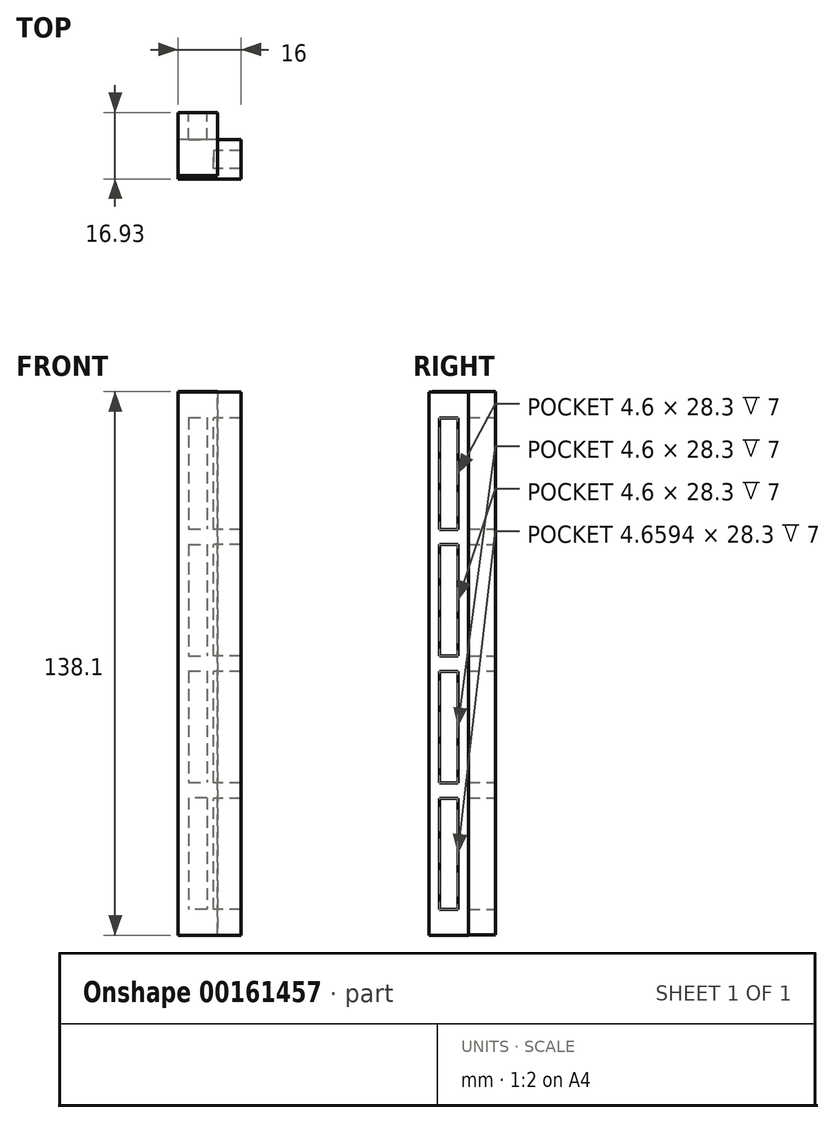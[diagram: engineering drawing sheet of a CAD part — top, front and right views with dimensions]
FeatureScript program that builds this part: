
annotation { "Feature Type Name" : "Feature", "Feature Type Description" : "" }
export const myFeature = defineFeature(function(context is Context, id is Id, definition is map)
    precondition{}
    {
        {
            var Q0;
            Q0=qCreatedBy(makeId("Front.planeOp"),FACE);
            var sketch = newSketch(context, id + "F0", { "sketchPlane" : qUnion([Q0])});
            skLineSegment(sketch, "E0.bottom", {"start": v(-30.25, 56.68) * mm, "end": v(-20.25, 56.68) * mm});
            skLineSegment(sketch, "E0.top", {"start": v(-30.25, -81.32) * mm, "end": v(-20.25, -81.32) * mm});
            skLineSegment(sketch, "E0.left", {"start": v(-30.25, 56.68) * mm, "end": v(-30.25, -81.32) * mm});
            skLineSegment(sketch, "E0.right", {"start": v(-20.25, 56.68) * mm, "end": v(-20.25, -81.32) * mm});
            skLineSegment(sketch, "E1.bottom", {"start": v(-27.56, 50.08) * mm, "end": v(-22.96, 50.08) * mm});
            skLineSegment(sketch, "E1.top", {"start": v(-27.56, 21.78) * mm, "end": v(-22.96, 21.78) * mm});
            skLineSegment(sketch, "E1.left", {"start": v(-27.56, 50.08) * mm, "end": v(-27.56, 21.78) * mm});
            skLineSegment(sketch, "E1.right", {"start": v(-22.96, 50.08) * mm, "end": v(-22.96, 21.78) * mm});
            skLineSegment(sketch, "E2", {"start": v(-26.53, 56.68) * mm, "end": v(-26.53, 50.08) * mm, "construction": true});
            skLineSegment(sketch, "E3", {"start": v(-27.56, 45.9) * mm, "end": v(-30.25, 45.9) * mm, "construction": true});
            skLineSegment(sketch, "E4", {"start": v(-22.96, 46.31) * mm, "end": v(-20.25, 46.31) * mm, "construction": true});
            skLineSegment(sketch, "E5", {"start": v(-25.26, 21.78) * mm, "end": v(-25.26, 17.88) * mm, "construction": true});
            skLineSegment(sketch, "E6", {"start": v(-27.56, 21.78) * mm, "end": v(-27.56, 17.88) * mm, "construction": true});
            skLineSegment(sketch, "E7", {"start": v(-22.96, 21.78) * mm, "end": v(-22.96, 17.88) * mm, "construction": true});
            skLineSegment(sketch, "E8.bottom", {"start": v(-27.56, 17.88) * mm, "end": v(-22.96, 17.88) * mm});
            skLineSegment(sketch, "E8.top", {"start": v(-27.56, -10.42) * mm, "end": v(-22.96, -10.42) * mm});
            skLineSegment(sketch, "E8.left", {"start": v(-27.56, 17.88) * mm, "end": v(-27.56, -10.42) * mm});
            skLineSegment(sketch, "E8.right", {"start": v(-22.96, 17.88) * mm, "end": v(-22.96, -10.42) * mm});
            skLineSegment(sketch, "E9", {"start": v(-22.96, -10.42) * mm, "end": v(-22.96, -14.32) * mm, "construction": true});
            skLineSegment(sketch, "E10", {"start": v(-27.56, -10.42) * mm, "end": v(-27.56, -14.32) * mm, "construction": true});
            skLineSegment(sketch, "E11.bottom", {"start": v(-27.56, -14.32) * mm, "end": v(-22.96, -14.32) * mm});
            skLineSegment(sketch, "E11.top", {"start": v(-27.56, -42.62) * mm, "end": v(-22.96, -42.62) * mm});
            skLineSegment(sketch, "E11.left", {"start": v(-27.56, -14.32) * mm, "end": v(-27.56, -42.62) * mm});
            skLineSegment(sketch, "E11.right", {"start": v(-22.96, -14.32) * mm, "end": v(-22.96, -42.62) * mm});
            skLineSegment(sketch, "E12", {"start": v(-27.56, -41.18) * mm, "end": v(-27.56, -42.62) * mm});
            skLineSegment(sketch, "E13", {"start": v(-22.96, -42.62) * mm, "end": v(-22.96, -46.52) * mm, "construction": true});
            skLineSegment(sketch, "E14.bottom", {"start": v(-22.96, -46.52) * mm, "end": v(-27.62, -46.52) * mm});
            skLineSegment(sketch, "E14.top", {"start": v(-22.96, -74.82) * mm, "end": v(-27.62, -74.82) * mm});
            skLineSegment(sketch, "E14.left", {"start": v(-22.96, -46.52) * mm, "end": v(-22.96, -74.82) * mm});
            skLineSegment(sketch, "E14.right", {"start": v(-27.62, -46.52) * mm, "end": v(-27.62, -74.82) * mm});
            skLineSegment(sketch, "E15", {"start": v(-22.96, -74.82) * mm, "end": v(-22.96, -81.32) * mm, "construction": true});
            skSolve(sketch);
        }
        {
            var Q0;
            Q0=makeQuery(id+"F0.imprint","IMPRINT",FACE,{"disambiguationData":[TD([[makeQuery(id+"F0.imprint","IMPRINT",EDGE,{"derivedFrom":sQuery(id+"F0.wireOp",EDGE,"E0.bottom")}),-1.0]])]});
            var Q1;
            Q1=makeQuery(id+"F0.imprint","IMPRINT",FACE,{"disambiguationData":[TD([[makeQuery(id+"F0.imprint","IMPRINT",EDGE,{"derivedFrom":sQuery(id+"F0.wireOp",EDGE,"E1.bottom")}),-1.0]])]});
            var Q2;
            Q2=makeQuery(id+"F0.imprint","IMPRINT",FACE,{"disambiguationData":[TD([[makeQuery(id+"F0.imprint","IMPRINT",EDGE,{"derivedFrom":sQuery(id+"F0.wireOp",EDGE,"E8.bottom")}),-1.0]])]});
            var Q3;
            Q3=makeQuery(id+"F0.imprint","IMPRINT",FACE,{"disambiguationData":[TD([[makeQuery(id+"F0.imprint","IMPRINT",EDGE,{"derivedFrom":sQuery(id+"F0.wireOp",EDGE,"E11.bottom")}),-1.0]])]});
            var Q4;
            Q4=makeQuery(id+"F0.imprint","IMPRINT",FACE,{"disambiguationData":[TD([[makeQuery(id+"F0.imprint","IMPRINT",EDGE,{"derivedFrom":sQuery(id+"F0.wireOp",EDGE,"E14.bottom")}),1.0]])]});
            extrude(context, id + "F1", {"entities" : qUnion([Q0, Q1, Q2, Q3, Q4]), "depth" : 16 * mm});
        }
        {
            var Q0;
            Q0=makeQuery(id+"F0.imprint","IMPRINT",FACE,{"disambiguationData":[TD([[makeQuery(id+"F0.imprint","IMPRINT",EDGE,{"derivedFrom":sQuery(id+"F0.wireOp",EDGE,"E1.bottom")}),-1.0]])]});
            var Q1;
            Q1=makeQuery(id+"F0.imprint","IMPRINT",FACE,{"disambiguationData":[TD([[makeQuery(id+"F0.imprint","IMPRINT",EDGE,{"derivedFrom":sQuery(id+"F0.wireOp",EDGE,"E8.bottom")}),-1.0]])]});
            var Q2;
            Q2=makeQuery(id+"F0.imprint","IMPRINT",FACE,{"disambiguationData":[TD([[makeQuery(id+"F0.imprint","IMPRINT",EDGE,{"derivedFrom":sQuery(id+"F0.wireOp",EDGE,"E11.bottom")}),-1.0]])]});
            var Q3;
            Q3=makeQuery(id+"F0.imprint","IMPRINT",FACE,{"disambiguationData":[TD([[makeQuery(id+"F0.imprint","IMPRINT",EDGE,{"derivedFrom":sQuery(id+"F0.wireOp",EDGE,"E14.bottom")}),1.0]])]});
            extrude(context, id + "F2", {"entities" : qUnion([Q0, Q1, Q2, Q3]), "operationType" : NewBodyOperationType.REMOVE, "depth" : 9 * mm});
        }
        {
            var Q0;
            {var subQ0=makeQuery(id+"F1.opExtrude","SWEPT_FACE",FACE,{"disambiguationData":[OSD([sQuery(id+"F0.wireOp",EDGE,"E0.right")])]});Q0=makeQuery(id+"FuPyKuqOHidPukL_1.boolean.opBoolean","MERGE",FACE,{"derivedFrom":[subQ0,makeQuery(id+"FuPyKuqOHidPukL_1.opPattern","COPY",FACE,{"derivedFrom":subQ0,"instanceName":"1"})]});}
            var sketch = newSketch(context, id + "F3", { "sketchPlane" : qUnion([Q0])});
            skLineSegment(sketch, "E16.bottom", {"start": v(-16.93, 56.58) * mm, "end": v(-6.93, 56.58) * mm});
            skLineSegment(sketch, "E16.top", {"start": v(-16.93, -81.42) * mm, "end": v(-6.93, -81.42) * mm});
            skLineSegment(sketch, "E16.left", {"start": v(-16.93, 56.58) * mm, "end": v(-16.93, -81.42) * mm});
            skLineSegment(sketch, "E16.right", {"start": v(-6.93, 56.58) * mm, "end": v(-6.93, -81.42) * mm});
            skLineSegment(sketch, "E17.bottom", {"start": v(-14.23, 49.98) * mm, "end": v(-9.63, 49.98) * mm});
            skLineSegment(sketch, "E17.top", {"start": v(-14.23, 21.68) * mm, "end": v(-9.63, 21.68) * mm});
            skLineSegment(sketch, "E17.left", {"start": v(-14.23, 49.98) * mm, "end": v(-14.23, 21.68) * mm});
            skLineSegment(sketch, "E17.right", {"start": v(-9.63, 49.98) * mm, "end": v(-9.63, 21.68) * mm});
            skLineSegment(sketch, "E18", {"start": v(-13.2, 56.58) * mm, "end": v(-13.2, 49.98) * mm, "construction": true});
            skLineSegment(sketch, "E19", {"start": v(-14.23, 45.8) * mm, "end": v(-16.93, 45.8) * mm, "construction": true});
            skLineSegment(sketch, "E20", {"start": v(-9.63, 46.2) * mm, "end": v(-6.93, 46.2) * mm, "construction": true});
            skLineSegment(sketch, "E21", {"start": v(-11.93, 21.68) * mm, "end": v(-11.93, 17.78) * mm, "construction": true});
            skLineSegment(sketch, "E22", {"start": v(-14.23, 21.68) * mm, "end": v(-14.23, 17.78) * mm, "construction": true});
            skLineSegment(sketch, "E23", {"start": v(-9.63, 21.68) * mm, "end": v(-9.63, 17.78) * mm, "construction": true});
            skLineSegment(sketch, "E24.bottom", {"start": v(-14.23, 17.78) * mm, "end": v(-9.63, 17.78) * mm});
            skLineSegment(sketch, "E24.top", {"start": v(-14.23, -10.52) * mm, "end": v(-9.63, -10.52) * mm});
            skLineSegment(sketch, "E24.left", {"start": v(-14.23, 17.78) * mm, "end": v(-14.23, -10.52) * mm});
            skLineSegment(sketch, "E24.right", {"start": v(-9.63, 17.78) * mm, "end": v(-9.63, -10.52) * mm});
            skLineSegment(sketch, "E25", {"start": v(-9.63, -10.52) * mm, "end": v(-9.63, -14.42) * mm, "construction": true});
            skLineSegment(sketch, "E26", {"start": v(-14.23, -10.52) * mm, "end": v(-14.23, -14.42) * mm, "construction": true});
            skLineSegment(sketch, "E27.bottom", {"start": v(-14.23, -14.42) * mm, "end": v(-9.63, -14.42) * mm});
            skLineSegment(sketch, "E27.top", {"start": v(-14.23, -42.72) * mm, "end": v(-9.63, -42.72) * mm});
            skLineSegment(sketch, "E27.left", {"start": v(-14.23, -14.42) * mm, "end": v(-14.23, -42.72) * mm});
            skLineSegment(sketch, "E27.right", {"start": v(-9.63, -14.42) * mm, "end": v(-9.63, -42.72) * mm});
            skLineSegment(sketch, "E28", {"start": v(-14.23, 18.57) * mm, "end": v(-14.23, -42.72) * mm});
            skLineSegment(sketch, "E29", {"start": v(-9.63, -42.72) * mm, "end": v(-9.63, -46.62) * mm, "construction": true});
            skLineSegment(sketch, "E30.bottom", {"start": v(-9.63, -46.62) * mm, "end": v(-14.3, -46.62) * mm});
            skLineSegment(sketch, "E30.top", {"start": v(-9.63, -74.92) * mm, "end": v(-14.3, -74.92) * mm});
            skLineSegment(sketch, "E30.left", {"start": v(-9.63, -46.62) * mm, "end": v(-9.63, -74.92) * mm});
            skLineSegment(sketch, "E30.right", {"start": v(-14.3, -46.62) * mm, "end": v(-14.3, -74.92) * mm});
            skLineSegment(sketch, "E31", {"start": v(-9.63, -74.92) * mm, "end": v(-9.63, -81.42) * mm, "construction": true});
            skSolve(sketch);
        }
        {
            var Q0;
            Q0=qSketchRegion(id+"F3",true);
            extrude(context, id + "F4", {"entities" : qUnion([Q0]), "operationType" : NewBodyOperationType.ADD, "depth" : 6 * mm, "hasSecondDirection" : true, "secondDirectionOppositeDirection" : true, "secondDirectionDepth" : 10 * mm});
        }
        {
            var Q0;
            {var subQ0=makeQuery(id+"F1.opExtrude","SWEPT_FACE",FACE,{"disambiguationData":[OSD([sQuery(id+"F0.wireOp",EDGE,"E0.right")])]});Q0=makeQuery(id+"F4.boolean.opBoolean","SPLIT",FACE,{"disambiguationData":[TD([makeQuery(id+"F4.opExtrude","SWEPT_FACE",FACE,{"disambiguationData":[OSD([sQuery(id+"F3.wireOp",EDGE,"E17.bottom")])]})])],"derivedFrom":makeQuery(id+"FuPyKuqOHidPukL_1.boolean.opBoolean","MERGE",FACE,{"derivedFrom":[subQ0,makeQuery(id+"FuPyKuqOHidPukL_1.opPattern","COPY",FACE,{"derivedFrom":subQ0,"instanceName":"1"})]})});}
            var Q1;
            {var subQ0=sQuery(id+"F3.wireOp",EDGE,"E24.bottom");var subQ3=makeQuery(id+"F1.opExtrude","SWEPT_FACE",FACE,{"disambiguationData":[OSD([sQuery(id+"F0.wireOp",EDGE,"E0.right")])]});Q1=makeQuery(id+"F4.boolean.opBoolean","SPLIT",FACE,{"disambiguationData":[TD([makeQuery(id+"F4.opExtrude","SWEPT_FACE",FACE,{"disambiguationData":[OSD([subQ0])]})])],"derivedFrom":makeQuery(id+"FuPyKuqOHidPukL_1.boolean.opBoolean","MERGE",FACE,{"derivedFrom":[subQ3,makeQuery(id+"FuPyKuqOHidPukL_1.opPattern","COPY",FACE,{"derivedFrom":subQ3,"instanceName":"1"})]})});}
            var Q2;
            {var subQ0=sQuery(id+"F3.wireOp",EDGE,"E27.bottom");var subQ3=makeQuery(id+"F1.opExtrude","SWEPT_FACE",FACE,{"disambiguationData":[OSD([sQuery(id+"F0.wireOp",EDGE,"E0.right")])]});Q2=makeQuery(id+"F4.boolean.opBoolean","SPLIT",FACE,{"disambiguationData":[TD([makeQuery(id+"F4.opExtrude","SWEPT_FACE",FACE,{"disambiguationData":[OSD([subQ0])]})])],"derivedFrom":makeQuery(id+"FuPyKuqOHidPukL_1.boolean.opBoolean","MERGE",FACE,{"derivedFrom":[subQ3,makeQuery(id+"FuPyKuqOHidPukL_1.opPattern","COPY",FACE,{"derivedFrom":subQ3,"instanceName":"1"})]})});}
            var Q3;
            {var subQ0=makeQuery(id+"F1.opExtrude","SWEPT_FACE",FACE,{"disambiguationData":[OSD([sQuery(id+"F0.wireOp",EDGE,"E0.right")])]});Q3=makeQuery(id+"F4.boolean.opBoolean","SPLIT",FACE,{"disambiguationData":[TD([makeQuery(id+"F4.opExtrude","SWEPT_FACE",FACE,{"disambiguationData":[OSD([sQuery(id+"F3.wireOp",EDGE,"E30.bottom")])]})])],"derivedFrom":makeQuery(id+"FuPyKuqOHidPukL_1.boolean.opBoolean","MERGE",FACE,{"derivedFrom":[subQ0,makeQuery(id+"FuPyKuqOHidPukL_1.opPattern","COPY",FACE,{"derivedFrom":subQ0,"instanceName":"1"})]})});}
            extrude(context, id + "F5", {"entities" : qUnion([Q0, Q1, Q2, Q3]), "operationType" : NewBodyOperationType.REMOVE, "oppositeDirection" : true, "depth" : 1 * mm});
        }
    });
